# Revit family: A6
name_source: partatom
category: Lighting Fixtures
revit_build: Autodesk Revit 2014 (Build: 20130308_1515(x64)
units: mm (PartAtom-declared; Revit-internal decimal feet)

## types (1)
- A6
    Apparent Load = 0 VA
    Certification = UL,CSA
    Color Filter = 16777215
    Default Elevation = 48"
    Description = 6 inch ADJUSTABLE DOWNLIGHTS
    Dimming Lamp Color Temperature Shift = <None>
    Features = 35º vertical and 362º rotational aiming
35º vertical aiming with visual aiming markers
All trims feature center beam optics
Hot aiming standard for all trims
Horizontal and vertical adjustment can be locked in position
B24 bar hangers sold separately for T-bar ceilings
    Finish = Steel
    Housing = Reflector
    Lamp = MR16
    Manufacturer = Prescolite
    Model = A6
    Photometric Web File = a6par306c3bat_6c3bat_30_degree_lamp.IES
    Photometric Web Link = https://www.hubbell.com
    Product Page URL = http://www.prescolite.com
    Product Specification Sheet = https://hubbellcdn.com
    Tilt Angle = -90.00°
    Type Comments = Lighting Fixture
    URL = https://www.hubbell.com
    Wattage Comments = 20-50 W

## geometry (parser evidence)
native form markers: Blend x4, Sweep x1
no freeform markers — native parametric forms only
